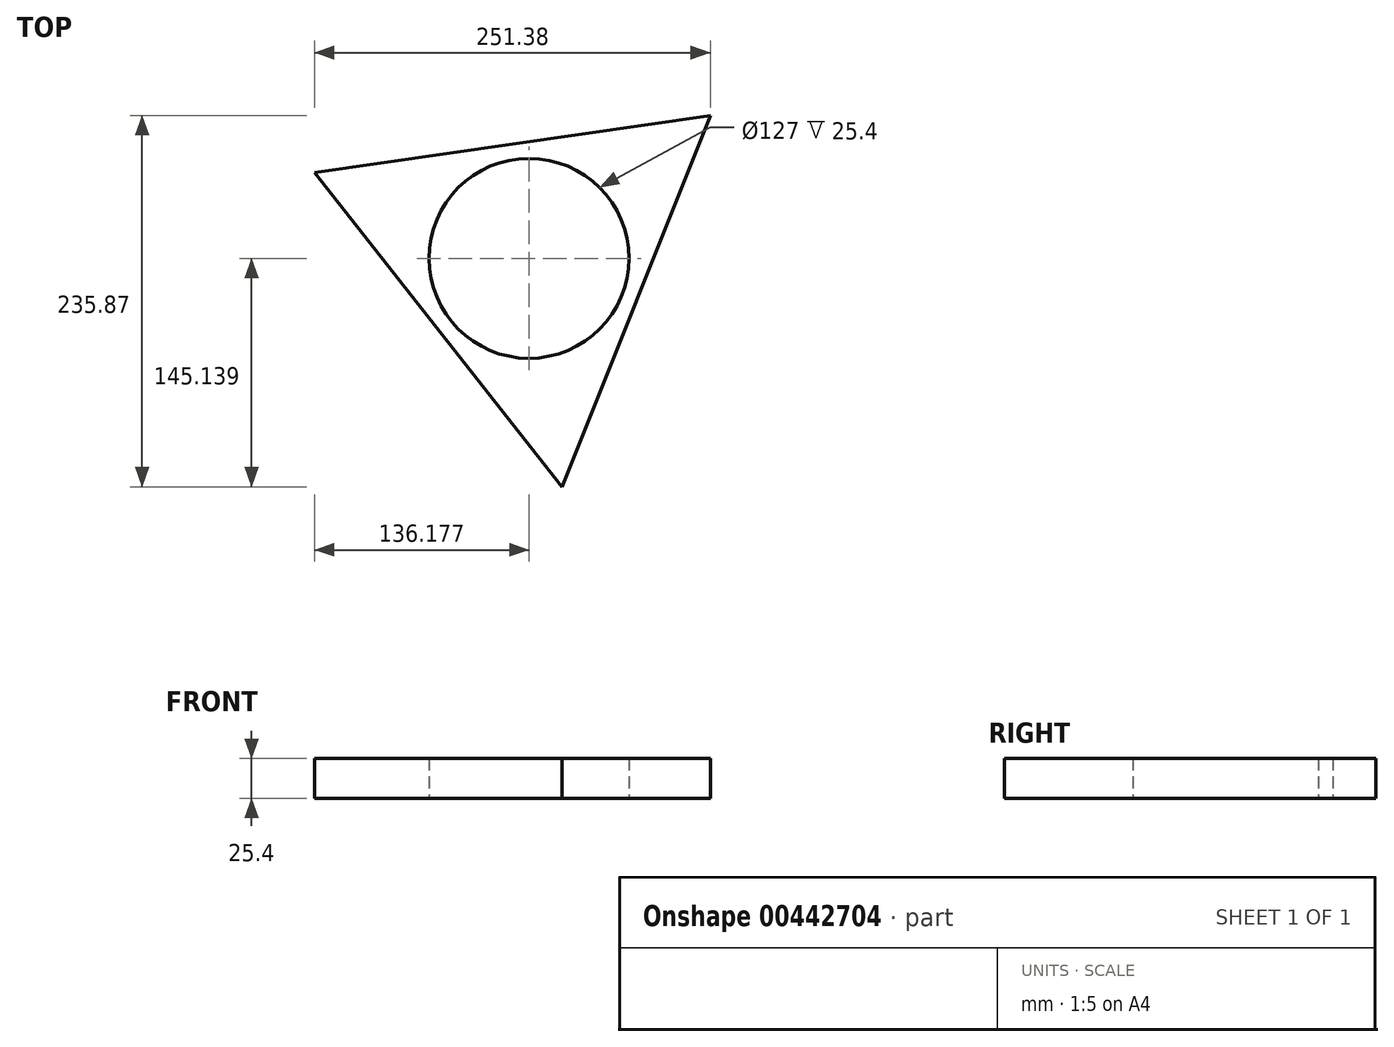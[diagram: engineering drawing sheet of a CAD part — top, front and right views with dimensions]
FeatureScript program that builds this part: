
annotation { "Feature Type Name" : "Feature", "Feature Type Description" : "" }
export const myFeature = defineFeature(function(context is Context, id is Id, definition is map)
    precondition{}
    {
        {
            var Q0;
            Q0=qCreatedBy(makeId("Top.planeOp"),FACE);
            var sketch = newSketch(context, id + "F0", { "sketchPlane" : qUnion([Q0])});
            skCircle(sketch, "E0.cCircle", {"center": v(-22.7, 32.92) * mm, "radius": 73.32 * mm, "construction": true});
            skLineSegment(sketch, "E0.0", {"start": v(-158.87, 87.33) * mm, "end": v(92.51, 123.65) * mm});
            skLineSegment(sketch, "E0.1", {"start": v(92.51, 123.65) * mm, "end": v(-1.72, -112.22) * mm});
            skLineSegment(sketch, "E0.2", {"start": v(-1.72, -112.22) * mm, "end": v(-158.87, 87.33) * mm});
            skPoint(sketch, "E0.0.midPoint", {"position": v(-33.18, 105.49) * mm});
            skCircle(sketch, "E1", {"center": v(-22.7, 32.92) * mm, "radius": 63.5 * mm});
            skSolve(sketch);
        }
        {
            var Q0;
            Q0=makeQuery(id+"F0.imprint","IMPRINT",FACE,{"disambiguationData":[TD([[makeQuery(id+"F0.imprint","IMPRINT",EDGE,{"derivedFrom":sQuery(id+"F0.wireOp",EDGE,"E0.0")}),-1.0]])]});
            extrude(context, id + "F1", {"entities" : qUnion([Q0]), "depth" : 25.4 * mm});
        }
    });
